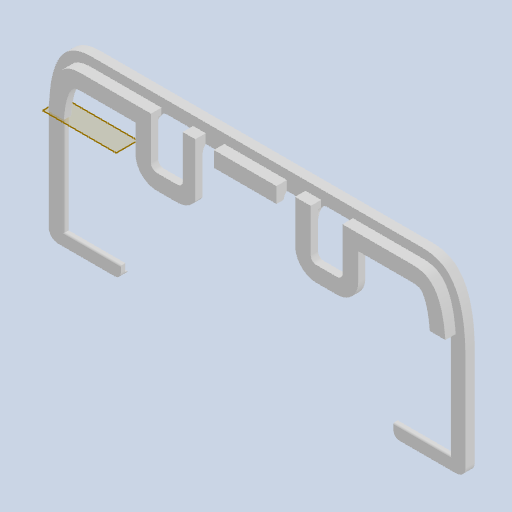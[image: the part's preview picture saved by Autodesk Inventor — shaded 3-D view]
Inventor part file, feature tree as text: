
AUTODESK INVENTOR PART (.ipt)
format: ipt  version: 2022 (Build 260153000, 153)  size: 805,888 bytes
history: native  units: mm
features: other x11, reference x7, extrude x5, sketch x5, fillet x5, projected_geometry x2, chamfer x1
ambient origin geometry x8: Origin, YZ Plane, XZ Plane, XY Plane, X Axis, Y Axis, Z Axis, Center Point
bodies: Body1 (feature_tree)
feature tree (36):
  other  "Твердое тело1"
  extrude  "Выдавливание1"  Depth=5.0mm
  sketch  "Эскиз2"
  other  "РабПлоскость1"
  other  "РабПлоскость2"
  other  "РабПлоскость3"
  extrude  "Выдавливание2"  Depth=5.0mm
  extrude  "Выдавливание3"  Depth=5.0mm
  extrude  "Выдавливание4"  Depth=0.2mm
  chamfer  "Фаска1"  Distance=0.2mm
  other  "РабПлоскость4"
  fillet  "Сопряжение1"  Radius=0.2mm
  sketch  "Эскиз6"
  other  "РабПлоскость5"
  extrude  "Выдавливание5"  Depth=5.0mm
  fillet  "Сопряжение2"  Radius=3.0mm
  fillet  "Сопряжение3"  Radius=3.3mm
  fillet  "Сопряжение4"  Radius=5.0mm
  fillet  "Сопряжение5"  Radius=5.0mm
  sketch  "Эскиз1"
  reference  "Ссылка2"
  reference  "Ссылка3"
  reference  "Ссылка4"
  reference  "Ссылка5"
  sketch  "Эскиз3"
  projected_geometry  "Спроецированная петля1"
  sketch  "Эскиз4"
  projected_geometry  "Спроецированная петля2"
  reference  "Ссылка8"
  reference  "Ссылка9"
  reference  "Ссылка10"
  other  "<userpath>\Documents\Git\MZCAT_2024\MZCAT_4.iam"
  other  "MZCAT_4.iam"
  other  "commutationCATboard:1"
  other  "motherboard_plate:1"
  other  "motherboard_key:1"
